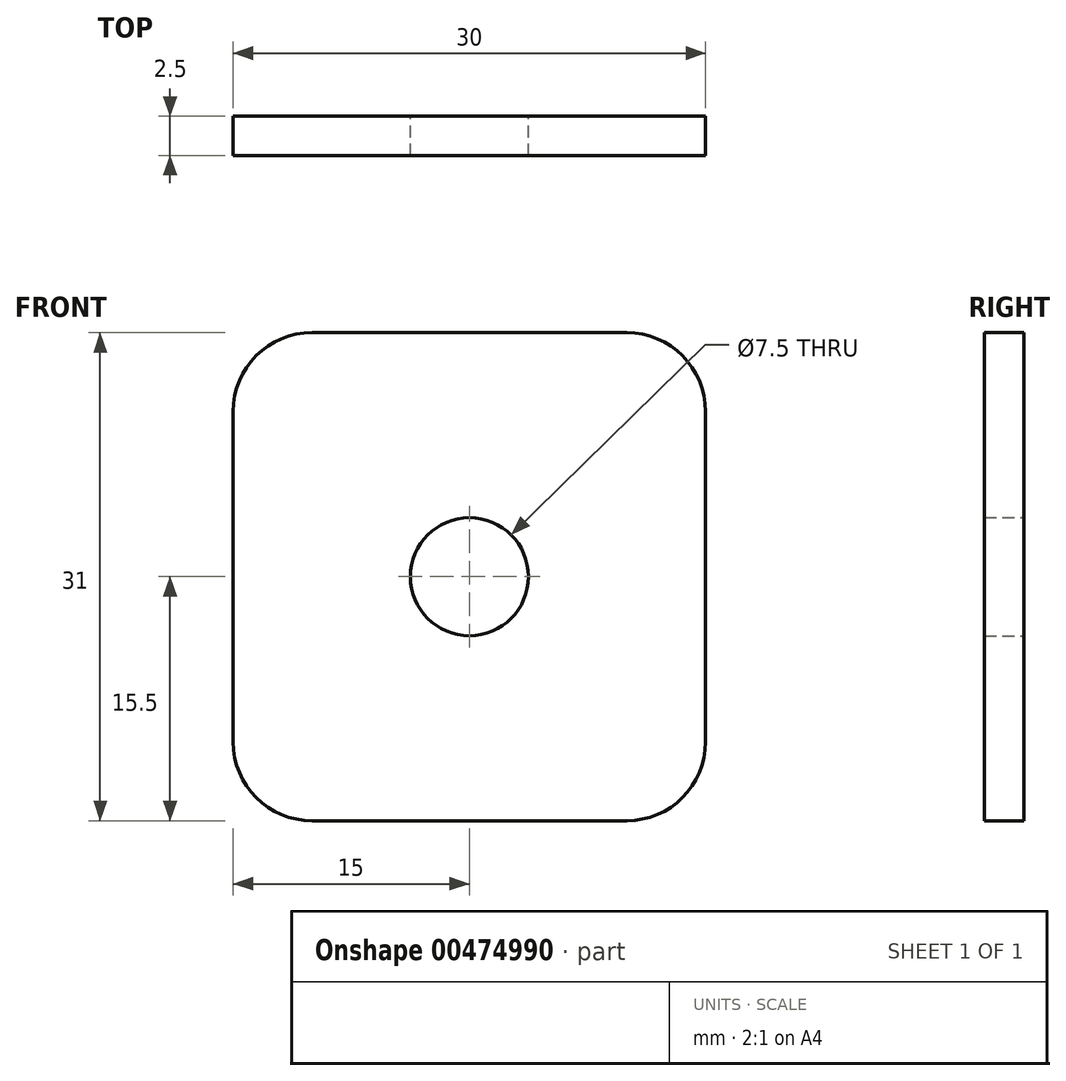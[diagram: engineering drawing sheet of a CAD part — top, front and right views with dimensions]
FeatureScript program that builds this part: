
annotation { "Feature Type Name" : "Feature", "Feature Type Description" : "" }
export const myFeature = defineFeature(function(context is Context, id is Id, definition is map)
    precondition{}
    {
        {
            var Q0;
            Q0=qCreatedBy(makeId("Front.planeOp"),FACE);
            var sketch = newSketch(context, id + "F0", { "sketchPlane" : qUnion([Q0])});
            skLineSegment(sketch, "E0.bottom", {"start": v(-15, 15.5) * mm, "end": v(15, 15.5) * mm});
            skLineSegment(sketch, "E0.top", {"start": v(-15, -15.5) * mm, "end": v(15, -15.5) * mm});
            skLineSegment(sketch, "E0.left", {"start": v(-15, 15.5) * mm, "end": v(-15, -15.5) * mm});
            skLineSegment(sketch, "E0.right", {"start": v(15, 15.5) * mm, "end": v(15, -15.5) * mm});
            skPoint(sketch, "E0.middle", {"position": v(0, 0) * mm});
            skCircle(sketch, "E1", {"center": v(0, 0) * mm, "radius": 3.75 * mm});
            skSolve(sketch);
        }
        {
            var Q0;
            Q0=qSketchRegion(id+"F0",true);
            extrude(context, id + "F1", {"entities" : qUnion([Q0]), "endBound" : BoundingType.SYMMETRIC, "depth" : 2.5 * mm});
        }
        {
            var Q0;
            Q0=makeQuery(id+"F1.opExtrude","SWEPT_EDGE",EDGE,{"disambiguationData":[OSD([sQuery(id+"F0.wireOp",EDGE,"E0.bottom"),sQuery(id+"F0.wireOp",EDGE,"E0.right")])]});
            var Q1;
            Q1=makeQuery(id+"F1.opExtrude","SWEPT_EDGE",EDGE,{"disambiguationData":[OSD([sQuery(id+"F0.wireOp",EDGE,"E0.top"),sQuery(id+"F0.wireOp",EDGE,"E0.right")])]});
            var Q2;
            Q2=makeQuery(id+"F1.opExtrude","SWEPT_EDGE",EDGE,{"disambiguationData":[OSD([sQuery(id+"F0.wireOp",EDGE,"E0.bottom"),sQuery(id+"F0.wireOp",EDGE,"E0.left")])]});
            var Q3;
            Q3=makeQuery(id+"F1.opExtrude","SWEPT_EDGE",EDGE,{"disambiguationData":[OSD([sQuery(id+"F0.wireOp",EDGE,"E0.top"),sQuery(id+"F0.wireOp",EDGE,"E0.left")])]});
            fillet(context, id + "F2", {"entities" : qUnion([Q0, Q1, Q2, Q3]), "radius" : 5 * mm, "tangentPropagation" : true, "allowEdgeOverflow" : false});
        }
    });
